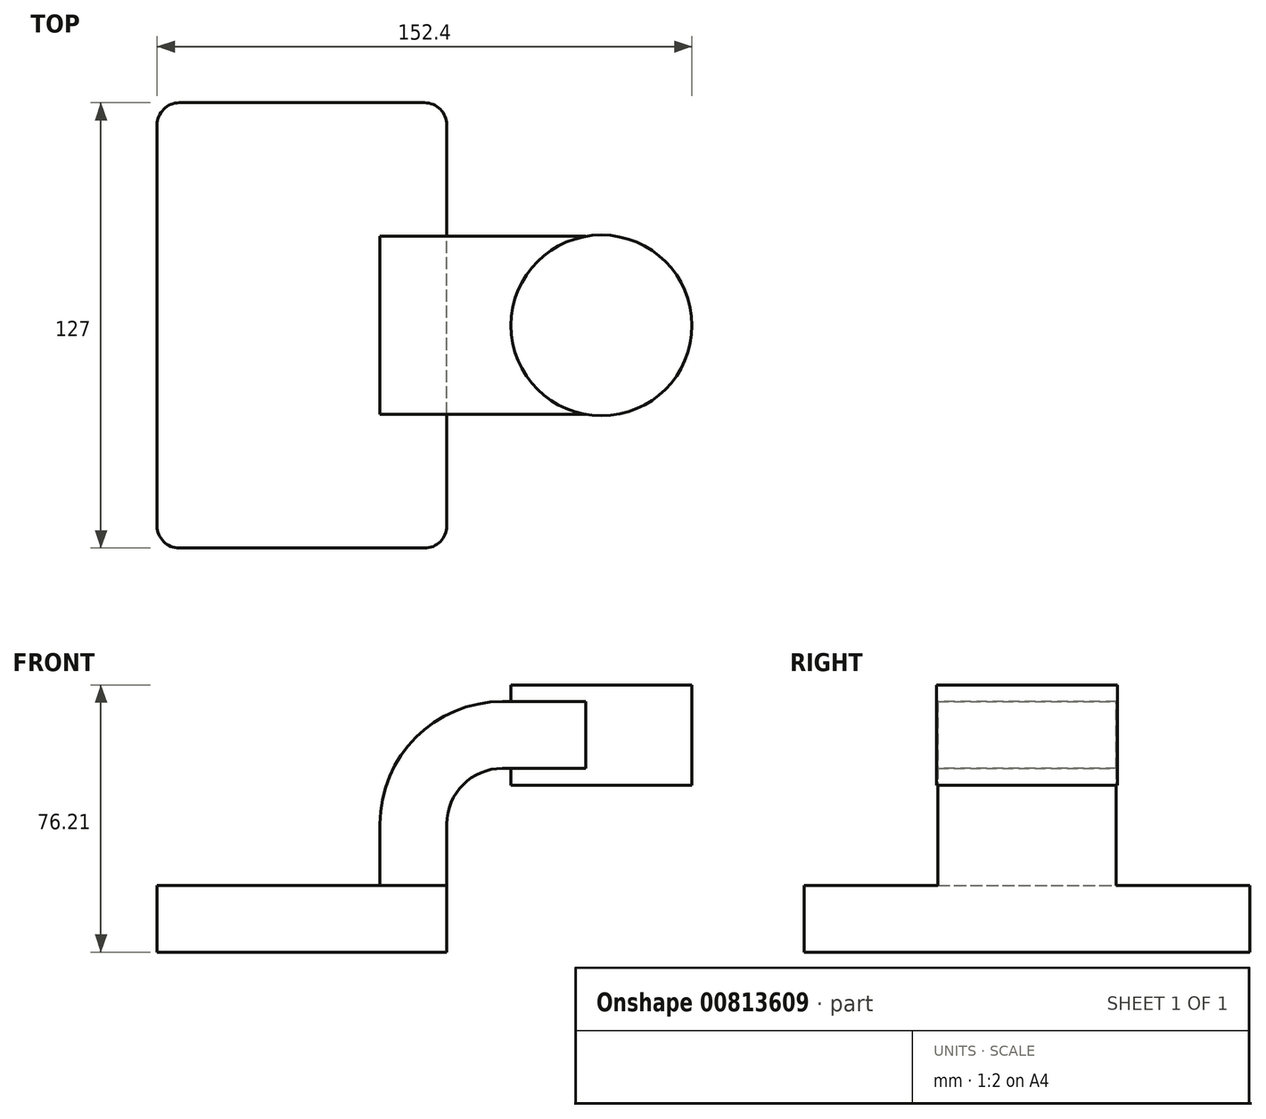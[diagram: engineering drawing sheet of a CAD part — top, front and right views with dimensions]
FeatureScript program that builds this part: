
annotation { "Feature Type Name" : "Feature", "Feature Type Description" : "" }
export const myFeature = defineFeature(function(context is Context, id is Id, definition is map)
    precondition{}
    {
        {
            var Q0;
            Q0=qCreatedBy(makeId("Front.planeOp"),FACE);
            var sketch = newSketch(context, id + "F0", { "sketchPlane" : qUnion([Q0])});
            skLineSegment(sketch, "E0.bottom", {"start": v(-41.27, 9.53) * mm, "end": v(41.28, 9.53) * mm});
            skLineSegment(sketch, "E0.top", {"start": v(-41.28, -9.53) * mm, "end": v(41.27, -9.53) * mm});
            skLineSegment(sketch, "E0.left", {"start": v(-41.28, 9.52) * mm, "end": v(-41.28, -9.52) * mm});
            skLineSegment(sketch, "E0.right", {"start": v(41.27, 9.53) * mm, "end": v(41.27, -9.52) * mm});
            skPoint(sketch, "E0.middle", {"position": v(0, 0) * mm});
            skLineSegment(sketch, "E1.bottom", {"start": v(60.33, 66.68) * mm, "end": v(111.12, 66.68) * mm});
            skLineSegment(sketch, "E1.top", {"start": v(60.33, 38.1) * mm, "end": v(111.12, 38.1) * mm});
            skLineSegment(sketch, "E1.left", {"start": v(60.33, 66.68) * mm, "end": v(60.33, 38.1) * mm});
            skLineSegment(sketch, "E1.right", {"start": v(111.12, 66.68) * mm, "end": v(111.12, 38.1) * mm});
            skPoint(sketch, "E1.middle", {"position": v(85.72, 52.39) * mm});
            skLineSegment(sketch, "E2", {"start": v(41.28, 9.53) * mm, "end": v(41.28, 27) * mm});
            skArc(sketch, "E3", {"start": v(41.28, 27) * mm, "mid": v(45.92, 38.23) * mm, "end": v(57.15, 42.88) * mm});
            skLineSegment(sketch, "E4", {"start": v(57.15, 42.88) * mm, "end": v(85.34, 42.88) * mm});
            skLineSegment(sketch, "E5.0", {"start": v(57.15, 61.93) * mm, "end": v(85.34, 61.93) * mm});
            skArc(sketch, "E5.1", {"start": v(22.23, 27) * mm, "mid": v(32.45, 51.7) * mm, "end": v(57.15, 61.93) * mm});
            skLineSegment(sketch, "E5.2", {"start": v(22.23, 9.53) * mm, "end": v(22.23, 27) * mm});
            skLineSegment(sketch, "E6", {"start": v(85.34, 66.68) * mm, "end": v(85.34, 38.1) * mm});
            skFitSpline(sketch, "E7", {"points": [v(57.15, 61.93) * mm, v(-41.28, 9.52) * mm], "startDerivative": vector(-182.6, 0.57) * mm, "endDerivative": vector(-9.7, -110.96) * mm});
            skSolve(sketch);
        }
        {
            var Q0;
            Q0=makeQuery(id+"F0.imprint","IMPRINT",FACE,{"disambiguationData":[TD([[makeQuery(id+"F0.imprint","IMPRINT",EDGE,{"derivedFrom":sQuery(id+"F0.wireOp",EDGE,"E0.top")}),1.0]])]});
            extrude(context, id + "F1", {"entities" : qUnion([Q0]), "endBound" : BoundingType.SYMMETRIC, "depth" : 127 * mm, "offsetDistance" : 25.4 * mm});
        }
        {
            var Q0;
            {var subQ1=sQuery(id+"F0.wireOp",EDGE,"E2");Q0=makeQuery(id+"F0.imprint","IMPRINT",FACE,{"disambiguationData":[TD([[makeQuery(id+"F0.imprint","IMPRINT",EDGE,{"derivedFrom":subQ1}),1.0]])]});}
            var Q1;
            {var subQ0=sQuery(id+"F0.wireOp",EDGE,"E5.0");var subQ1=sQuery(id+"F0.wireOp",EDGE,"E1.left");var subQ2=makeQuery(id+"F0.imprint","INTERSECT",VERTEX,{"derivedFrom":[subQ1,subQ0]});Q1=makeQuery(id+"F0.imprint","IMPRINT",FACE,{"disambiguationData":[TD([[makeQuery(id+"F0.imprint","IMPRINT",EDGE,{"disambiguationData":[TD([[subQ2,-1.0]])],"derivedFrom":subQ1}),1.0]])]});}
            extrude(context, id + "F2", {"entities" : qUnion([Q0, Q1]), "operationType" : NewBodyOperationType.ADD, "endBound" : BoundingType.SYMMETRIC, "depth" : 50.8 * mm, "offsetDistance" : 25.4 * mm});
        }
        {
            var Q0;
            Q0=makeQuery(id+"F0.imprint","IMPRINT",FACE,{"disambiguationData":[TD([[makeQuery(id+"F0.imprint","IMPRINT",EDGE,{"derivedFrom":sQuery(id+"F0.wireOp",EDGE,"E5.1")}),1.0]])]});
            extrude(context, id + "F3", {"entities" : qUnion([Q0]), "operationType" : NewBodyOperationType.ADD, "depth" : 15.88 * mm, "offsetDistance" : 25.4 * mm});
        }
        {
            var Q0;
            {var subQ0=sQuery(id+"F0.wireOp",EDGE,"E1.right");Q0=makeQuery(id+"F0.imprint","IMPRINT",FACE,{"disambiguationData":[TD([[makeQuery(id+"F0.imprint","IMPRINT",EDGE,{"derivedFrom":subQ0}),-1.0]])]});}
            var Q1;
            Q1=sQuery(id+"F0.wireOp",EDGE,"E6");
            revolve(context, id + "F4", {"operationType" : NewBodyOperationType.ADD, "surfaceOperationType" : NewSurfaceOperationType.NEW, "entities" : qUnion([Q0]), "axis" : qUnion([Q1]), "revolveType" : RevolveType.FULL});
        }
        {
            var Q0;
            Q0=makeQuery(id+"F1.opExtrude","CAP_EDGE",EDGE,{"disambiguationData":[OSD([sQuery(id+"F0.wireOp",EDGE,"E0.left")])],"isStart":true});
            var Q1;
            Q1=makeQuery(id+"F1.opExtrude","CAP_EDGE",EDGE,{"disambiguationData":[OSD([sQuery(id+"F0.wireOp",EDGE,"E0.right")])],"isStart":true});
            var Q2;
            Q2=makeQuery(id+"F1.opExtrude","CAP_EDGE",EDGE,{"disambiguationData":[OSD([sQuery(id+"F0.wireOp",EDGE,"E0.right")])],"isStart":false});
            var Q3;
            Q3=makeQuery(id+"F1.opExtrude","CAP_EDGE",EDGE,{"disambiguationData":[OSD([sQuery(id+"F0.wireOp",EDGE,"E0.left")])],"isStart":false});
            fillet(context, id + "F5", {"entities" : qUnion([Q0, Q1, Q2, Q3]), "radius" : 6.35 * mm, "tangentPropagation" : true, "allowEdgeOverflow" : false});
        }
    });
